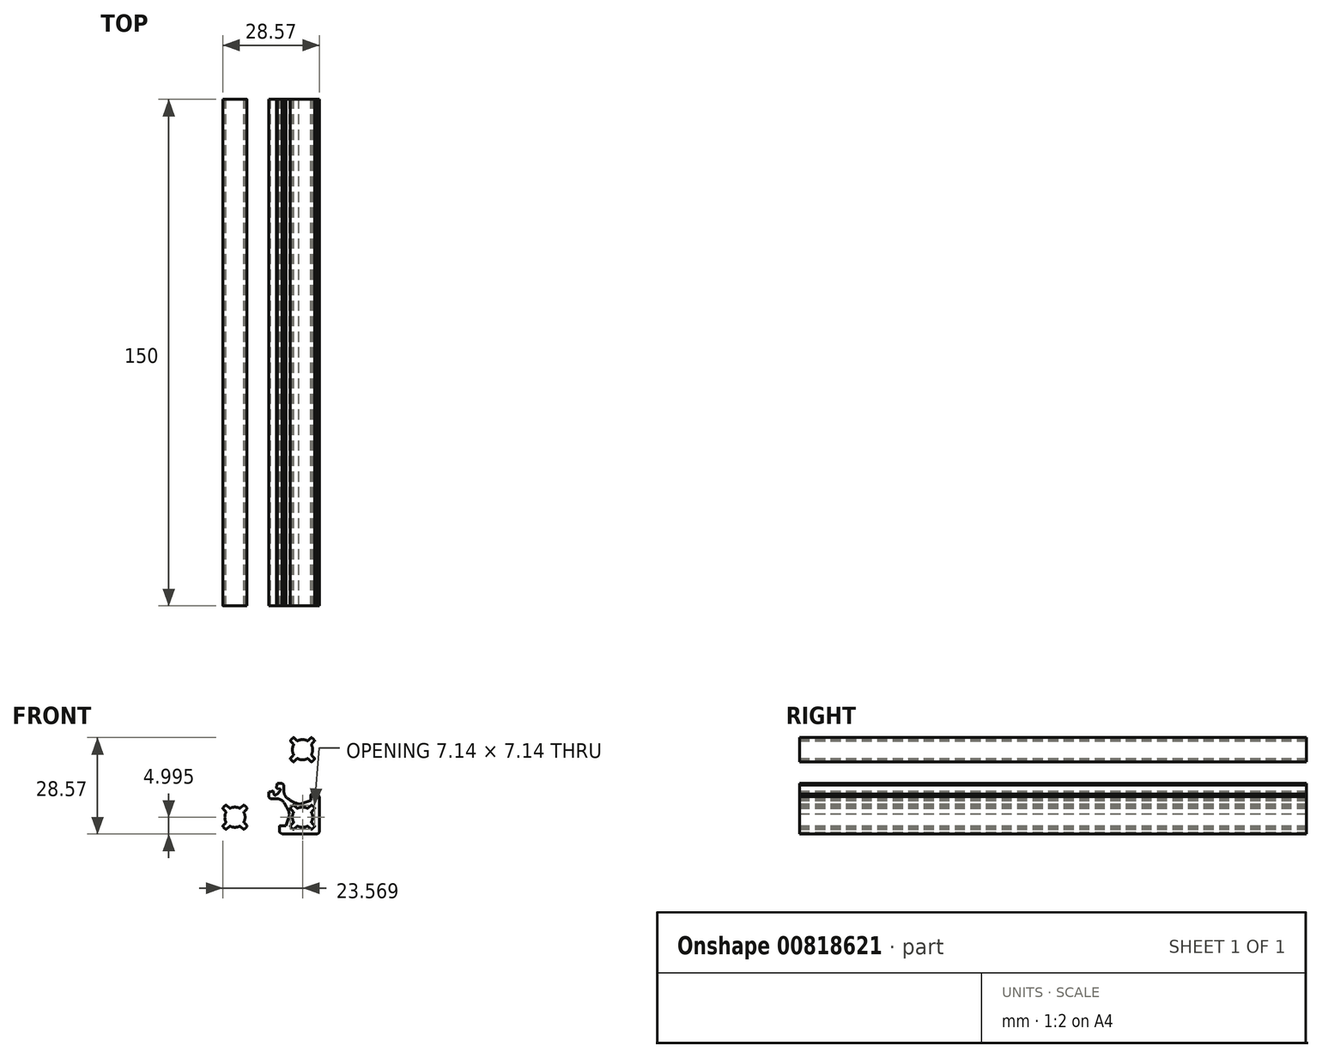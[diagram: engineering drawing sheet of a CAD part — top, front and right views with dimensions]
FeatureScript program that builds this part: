
annotation { "Feature Type Name" : "Feature", "Feature Type Description" : "" }
export const myFeature = defineFeature(function(context is Context, id is Id, definition is map)
    precondition{}
    {
        {
            var Q0;
            Q0=qCreatedBy(makeId("Front.planeOp"),FACE);
            var sketch = newSketch(context, id + "F0", { "sketchPlane" : qUnion([Q0])});
            skLineSegment(sketch, "E0", {"start": v(-2.82, -20.25) * mm, "end": v(-2.82, -15.85) * mm});
            skLineSegment(sketch, "E1", {"start": v(-5.02, -18.05) * mm, "end": v(-0.62, -18.05) * mm});
            skArc(sketch, "E2", {"start": v(-5.5, -19.39) * mm, "mid": v(-5.48, -19.57) * mm, "end": v(-5.56, -19.74) * mm});
            skLineSegment(sketch, "E3", {"start": v(-5.56, -19.74) * mm, "end": v(-6.3, -20.48) * mm});
            skArc(sketch, "E4", {"start": v(-6.3, -20.48) * mm, "mid": v(-6.4, -20.67) * mm, "end": v(-6.32, -20.88) * mm});
            skArc(sketch, "E5", {"start": v(-6.32, -20.88) * mm, "mid": v(-6, -21.24) * mm, "end": v(-5.64, -21.56) * mm});
            skArc(sketch, "E6", {"start": v(-5.64, -21.56) * mm, "mid": v(-5.44, -21.62) * mm, "end": v(-5.24, -21.54) * mm});
            skLineSegment(sketch, "E7", {"start": v(-5.24, -21.54) * mm, "end": v(-4.5, -20.8) * mm});
            skArc(sketch, "E8", {"start": v(-4.5, -20.8) * mm, "mid": v(-4.34, -20.71) * mm, "end": v(-4.16, -20.74) * mm});
            skArc(sketch, "E9", {"start": v(-4.16, -20.74) * mm, "mid": v(-2.82, -21.05) * mm, "end": v(-1.48, -20.74) * mm});
            skArc(sketch, "E10", {"start": v(-1.48, -20.74) * mm, "mid": v(-1.3, -20.71) * mm, "end": v(-1.14, -20.8) * mm});
            skLineSegment(sketch, "E11", {"start": v(-1.14, -20.8) * mm, "end": v(-0.4, -21.54) * mm});
            skArc(sketch, "E12", {"start": v(-0.4, -21.54) * mm, "mid": v(-0.2, -21.62) * mm, "end": v(0, -21.56) * mm});
            skArc(sketch, "E13", {"start": v(0, -21.56) * mm, "mid": v(0.36, -21.24) * mm, "end": v(0.68, -20.88) * mm});
            skArc(sketch, "E14", {"start": v(0.68, -20.88) * mm, "mid": v(0.75, -20.67) * mm, "end": v(0.66, -20.48) * mm});
            skLineSegment(sketch, "E15", {"start": v(0.66, -20.48) * mm, "end": v(-0.08, -19.74) * mm});
            skArc(sketch, "E16", {"start": v(-0.08, -19.74) * mm, "mid": v(-0.16, -19.57) * mm, "end": v(-0.13, -19.39) * mm});
            skArc(sketch, "E17", {"start": v(-0.13, -19.39) * mm, "mid": v(0.18, -18.05) * mm, "end": v(-0.13, -16.72) * mm});
            skArc(sketch, "E18", {"start": v(-0.13, -16.72) * mm, "mid": v(-0.16, -16.54) * mm, "end": v(-0.08, -16.37) * mm});
            skLineSegment(sketch, "E19", {"start": v(-0.08, -16.37) * mm, "end": v(0.66, -15.63) * mm});
            skArc(sketch, "E20", {"start": v(0.66, -15.63) * mm, "mid": v(0.75, -15.44) * mm, "end": v(0.68, -15.23) * mm});
            skArc(sketch, "E21", {"start": v(0.68, -15.23) * mm, "mid": v(0.36, -14.87) * mm, "end": v(0, -14.55) * mm});
            skArc(sketch, "E22", {"start": v(0, -14.55) * mm, "mid": v(-0.2, -14.48) * mm, "end": v(-0.4, -14.57) * mm});
            skLineSegment(sketch, "E23", {"start": v(-0.4, -14.57) * mm, "end": v(-1.14, -15.31) * mm});
            skArc(sketch, "E24", {"start": v(-1.14, -15.31) * mm, "mid": v(-1.3, -15.4) * mm, "end": v(-1.48, -15.37) * mm});
            skArc(sketch, "E25", {"start": v(-1.48, -15.37) * mm, "mid": v(-2.82, -15.05) * mm, "end": v(-4.16, -15.37) * mm});
            skArc(sketch, "E26", {"start": v(-4.16, -15.37) * mm, "mid": v(-4.34, -15.4) * mm, "end": v(-4.5, -15.31) * mm});
            skLineSegment(sketch, "E27", {"start": v(-4.5, -15.31) * mm, "end": v(-5.24, -14.57) * mm});
            skArc(sketch, "E28", {"start": v(-5.24, -14.57) * mm, "mid": v(-5.44, -14.48) * mm, "end": v(-5.64, -14.55) * mm});
            skArc(sketch, "E29", {"start": v(-5.64, -14.55) * mm, "mid": v(-6, -14.87) * mm, "end": v(-6.32, -15.23) * mm});
            skArc(sketch, "E30", {"start": v(-6.32, -15.23) * mm, "mid": v(-6.4, -15.44) * mm, "end": v(-6.3, -15.63) * mm});
            skLineSegment(sketch, "E31", {"start": v(-6.3, -15.63) * mm, "end": v(-5.56, -16.37) * mm});
            skArc(sketch, "E32", {"start": v(-5.56, -16.37) * mm, "mid": v(-5.48, -16.54) * mm, "end": v(-5.5, -16.72) * mm});
            skArc(sketch, "E33", {"start": v(-5.5, -16.72) * mm, "mid": v(-5.82, -18.05) * mm, "end": v(-5.5, -19.39) * mm});
            skLineSegment(sketch, "E34", {"start": v(-5.02, -38.05) * mm, "end": v(-0.62, -38.05) * mm});
            skLineSegment(sketch, "E35", {"start": v(-2.82, -35.85) * mm, "end": v(-2.82, -40.25) * mm});
            skArc(sketch, "E36", {"start": v(-5.5, -36.72) * mm, "mid": v(-5.48, -36.54) * mm, "end": v(-5.56, -36.37) * mm});
            skLineSegment(sketch, "E37", {"start": v(-5.56, -36.37) * mm, "end": v(-6.3, -35.63) * mm});
            skArc(sketch, "E38", {"start": v(-6.3, -35.63) * mm, "mid": v(-6.4, -35.44) * mm, "end": v(-6.33, -35.23) * mm});
            skArc(sketch, "E39", {"start": v(-6.33, -35.23) * mm, "mid": v(-6, -34.87) * mm, "end": v(-5.64, -34.55) * mm});
            skArc(sketch, "E40", {"start": v(-5.64, -34.55) * mm, "mid": v(-5.44, -34.48) * mm, "end": v(-5.24, -34.57) * mm});
            skLineSegment(sketch, "E41", {"start": v(-5.24, -34.57) * mm, "end": v(-4.5, -35.31) * mm});
            skArc(sketch, "E42", {"start": v(-4.5, -35.31) * mm, "mid": v(-4.34, -35.4) * mm, "end": v(-4.16, -35.37) * mm});
            skArc(sketch, "E43", {"start": v(-4.16, -35.37) * mm, "mid": v(-2.82, -35.05) * mm, "end": v(-1.48, -35.37) * mm});
            skArc(sketch, "E44", {"start": v(-1.48, -35.37) * mm, "mid": v(-1.3, -35.4) * mm, "end": v(-1.14, -35.31) * mm});
            skLineSegment(sketch, "E45", {"start": v(-1.14, -35.31) * mm, "end": v(-0.4, -34.57) * mm});
            skArc(sketch, "E46", {"start": v(-0.4, -34.57) * mm, "mid": v(-0.2, -34.48) * mm, "end": v(0, -34.55) * mm});
            skArc(sketch, "E47", {"start": v(0, -34.55) * mm, "mid": v(0.36, -34.87) * mm, "end": v(0.68, -35.23) * mm});
            skArc(sketch, "E48", {"start": v(0.68, -35.23) * mm, "mid": v(0.75, -35.44) * mm, "end": v(0.66, -35.63) * mm});
            skLineSegment(sketch, "E49", {"start": v(0.66, -35.63) * mm, "end": v(-0.08, -36.37) * mm});
            skArc(sketch, "E50", {"start": v(-0.08, -36.37) * mm, "mid": v(-0.16, -36.54) * mm, "end": v(-0.13, -36.72) * mm});
            skArc(sketch, "E51", {"start": v(-0.13, -36.72) * mm, "mid": v(0.18, -38.05) * mm, "end": v(-0.14, -39.4) * mm});
            skArc(sketch, "E52", {"start": v(-0.14, -39.4) * mm, "mid": v(-0.16, -39.57) * mm, "end": v(-0.08, -39.74) * mm});
            skLineSegment(sketch, "E53", {"start": v(-0.08, -39.74) * mm, "end": v(0.66, -40.48) * mm});
            skArc(sketch, "E54", {"start": v(0.66, -40.48) * mm, "mid": v(0.75, -40.67) * mm, "end": v(0.68, -40.88) * mm});
            skArc(sketch, "E55", {"start": v(0.68, -40.88) * mm, "mid": v(0.36, -41.24) * mm, "end": v(0, -41.56) * mm});
            skArc(sketch, "E56", {"start": v(0, -41.56) * mm, "mid": v(-0.2, -41.63) * mm, "end": v(-0.4, -41.54) * mm});
            skLineSegment(sketch, "E57", {"start": v(-0.4, -41.54) * mm, "end": v(-1.14, -40.8) * mm});
            skArc(sketch, "E58", {"start": v(-1.14, -40.8) * mm, "mid": v(-1.3, -40.71) * mm, "end": v(-1.49, -40.74) * mm});
            skArc(sketch, "E59", {"start": v(-1.49, -40.74) * mm, "mid": v(-2.82, -41.05) * mm, "end": v(-4.16, -40.74) * mm});
            skArc(sketch, "E60", {"start": v(-4.16, -40.74) * mm, "mid": v(-4.34, -40.71) * mm, "end": v(-4.5, -40.8) * mm});
            skLineSegment(sketch, "E61", {"start": v(-4.5, -40.8) * mm, "end": v(-5.24, -41.54) * mm});
            skArc(sketch, "E62", {"start": v(-5.24, -41.54) * mm, "mid": v(-5.44, -41.62) * mm, "end": v(-5.64, -41.56) * mm});
            skArc(sketch, "E63", {"start": v(-5.64, -41.56) * mm, "mid": v(-6, -41.24) * mm, "end": v(-6.33, -40.88) * mm});
            skArc(sketch, "E64", {"start": v(-6.33, -40.88) * mm, "mid": v(-6.4, -40.67) * mm, "end": v(-6.3, -40.48) * mm});
            skLineSegment(sketch, "E65", {"start": v(-6.3, -40.48) * mm, "end": v(-5.56, -39.74) * mm});
            skArc(sketch, "E66", {"start": v(-5.56, -39.74) * mm, "mid": v(-5.48, -39.57) * mm, "end": v(-5.5, -39.4) * mm});
            skArc(sketch, "E67", {"start": v(-5.5, -39.4) * mm, "mid": v(-5.82, -38.05) * mm, "end": v(-5.5, -36.72) * mm});
            skArc(sketch, "E68", {"start": v(-20.13, -36.72) * mm, "mid": v(-20.16, -36.54) * mm, "end": v(-20.07, -36.37) * mm});
            skLineSegment(sketch, "E69", {"start": v(-20.07, -36.37) * mm, "end": v(-19.33, -35.63) * mm});
            skArc(sketch, "E70", {"start": v(-19.33, -35.63) * mm, "mid": v(-19.25, -35.44) * mm, "end": v(-19.31, -35.23) * mm});
            skArc(sketch, "E71", {"start": v(-19.31, -35.23) * mm, "mid": v(-19.64, -34.87) * mm, "end": v(-20, -34.55) * mm});
            skArc(sketch, "E72", {"start": v(-20, -34.55) * mm, "mid": v(-20.2, -34.48) * mm, "end": v(-20.4, -34.57) * mm});
            skLineSegment(sketch, "E73", {"start": v(-20.4, -34.57) * mm, "end": v(-21.14, -35.31) * mm});
            skArc(sketch, "E74", {"start": v(-21.14, -35.31) * mm, "mid": v(-21.3, -35.4) * mm, "end": v(-21.48, -35.37) * mm});
            skArc(sketch, "E75", {"start": v(-21.48, -35.37) * mm, "mid": v(-22.82, -35.05) * mm, "end": v(-24.15, -35.37) * mm});
            skArc(sketch, "E76", {"start": v(-24.15, -35.37) * mm, "mid": v(-24.34, -35.4) * mm, "end": v(-24.5, -35.31) * mm});
            skLineSegment(sketch, "E77", {"start": v(-24.5, -35.31) * mm, "end": v(-25.24, -34.57) * mm});
            skArc(sketch, "E78", {"start": v(-25.24, -34.57) * mm, "mid": v(-25.44, -34.48) * mm, "end": v(-25.64, -34.55) * mm});
            skArc(sketch, "E79", {"start": v(-25.64, -34.55) * mm, "mid": v(-26, -34.87) * mm, "end": v(-26.32, -35.23) * mm});
            skArc(sketch, "E80", {"start": v(-26.32, -35.23) * mm, "mid": v(-26.39, -35.44) * mm, "end": v(-26.3, -35.63) * mm});
            skLineSegment(sketch, "E81", {"start": v(-26.3, -35.63) * mm, "end": v(-25.56, -36.37) * mm});
            skArc(sketch, "E82", {"start": v(-25.56, -36.37) * mm, "mid": v(-25.48, -36.54) * mm, "end": v(-25.5, -36.72) * mm});
            skArc(sketch, "E83", {"start": v(-25.5, -36.72) * mm, "mid": v(-25.82, -38.05) * mm, "end": v(-25.5, -39.4) * mm});
            skArc(sketch, "E84", {"start": v(-25.5, -39.4) * mm, "mid": v(-25.48, -39.57) * mm, "end": v(-25.56, -39.74) * mm});
            skLineSegment(sketch, "E85", {"start": v(-25.56, -39.74) * mm, "end": v(-26.3, -40.48) * mm});
            skArc(sketch, "E86", {"start": v(-26.3, -40.48) * mm, "mid": v(-26.39, -40.67) * mm, "end": v(-26.32, -40.88) * mm});
            skArc(sketch, "E87", {"start": v(-26.32, -40.88) * mm, "mid": v(-26, -41.24) * mm, "end": v(-25.64, -41.56) * mm});
            skArc(sketch, "E88", {"start": v(-25.64, -41.56) * mm, "mid": v(-25.44, -41.63) * mm, "end": v(-25.24, -41.54) * mm});
            skLineSegment(sketch, "E89", {"start": v(-25.24, -41.54) * mm, "end": v(-24.5, -40.8) * mm});
            skArc(sketch, "E90", {"start": v(-24.5, -40.8) * mm, "mid": v(-24.33, -40.71) * mm, "end": v(-24.15, -40.74) * mm});
            skArc(sketch, "E91", {"start": v(-24.15, -40.74) * mm, "mid": v(-22.82, -41.05) * mm, "end": v(-21.48, -40.74) * mm});
            skArc(sketch, "E92", {"start": v(-21.48, -40.74) * mm, "mid": v(-21.3, -40.71) * mm, "end": v(-21.14, -40.8) * mm});
            skLineSegment(sketch, "E93", {"start": v(-21.14, -40.8) * mm, "end": v(-20.4, -41.54) * mm});
            skArc(sketch, "E94", {"start": v(-20.4, -41.54) * mm, "mid": v(-20.2, -41.62) * mm, "end": v(-20, -41.56) * mm});
            skArc(sketch, "E95", {"start": v(-20, -41.56) * mm, "mid": v(-19.63, -41.24) * mm, "end": v(-19.31, -40.88) * mm});
            skArc(sketch, "E96", {"start": v(-19.31, -40.88) * mm, "mid": v(-19.25, -40.67) * mm, "end": v(-19.33, -40.48) * mm});
            skLineSegment(sketch, "E97", {"start": v(-19.33, -40.48) * mm, "end": v(-20.07, -39.74) * mm});
            skArc(sketch, "E98", {"start": v(-20.07, -39.74) * mm, "mid": v(-20.16, -39.57) * mm, "end": v(-20.13, -39.4) * mm});
            skArc(sketch, "E99", {"start": v(-20.13, -39.4) * mm, "mid": v(-19.82, -38.05) * mm, "end": v(-20.13, -36.72) * mm});
            skLineSegment(sketch, "E100", {"start": v(-22.82, -35.85) * mm, "end": v(-22.82, -40.25) * mm});
            skLineSegment(sketch, "E101", {"start": v(-20.62, -38.05) * mm, "end": v(-25.02, -38.05) * mm});
            skLineSegment(sketch, "E102", {"start": v(-20.62, -18.05) * mm, "end": v(-25.02, -18.05) * mm});
            skLineSegment(sketch, "E103", {"start": v(-22.82, -20.25) * mm, "end": v(-22.82, -15.85) * mm});
            skLineSegment(sketch, "E104", {"start": v(2.64, -28.05) * mm, "end": v(-29.04, -28.05) * mm});
            skLineSegment(sketch, "E105", {"start": v(-12.82, -44) * mm, "end": v(-12.82, -12.06) * mm});
            skArc(sketch, "E106", {"start": v(-9.58, -26.47) * mm, "mid": v(-9.36, -26.3) * mm, "end": v(-9.38, -26.02) * mm});
            skArc(sketch, "E107", {"start": v(-9.38, -26.02) * mm, "mid": v(-10, -25.23) * mm, "end": v(-10.78, -24.61) * mm});
            skArc(sketch, "E108", {"start": v(-10.78, -24.61) * mm, "mid": v(-11.06, -24.6) * mm, "end": v(-11.23, -24.82) * mm});
            skLineSegment(sketch, "E109", {"start": v(-11.23, -24.82) * mm, "end": v(-11.37, -25.56) * mm});
            skArc(sketch, "E110", {"start": v(-11.37, -25.56) * mm, "mid": v(-11.52, -25.77) * mm, "end": v(-11.78, -25.78) * mm});
            skArc(sketch, "E111", {"start": v(-11.78, -25.78) * mm, "mid": v(-12.82, -25.55) * mm, "end": v(-13.85, -25.78) * mm});
            skArc(sketch, "E112", {"start": v(-13.85, -25.78) * mm, "mid": v(-14.11, -25.77) * mm, "end": v(-14.27, -25.56) * mm});
            skLineSegment(sketch, "E113", {"start": v(-14.27, -25.56) * mm, "end": v(-14.4, -24.82) * mm});
            skArc(sketch, "E114", {"start": v(-14.4, -24.82) * mm, "mid": v(-14.57, -24.6) * mm, "end": v(-14.85, -24.61) * mm});
            skArc(sketch, "E115", {"start": v(-14.85, -24.61) * mm, "mid": v(-15.65, -25.23) * mm, "end": v(-16.26, -26.02) * mm});
            skArc(sketch, "E116", {"start": v(-16.26, -26.02) * mm, "mid": v(-16.27, -26.3) * mm, "end": v(-16.06, -26.47) * mm});
            skLineSegment(sketch, "E117", {"start": v(-16.06, -26.47) * mm, "end": v(-15.31, -26.6) * mm});
            skArc(sketch, "E118", {"start": v(-15.31, -26.6) * mm, "mid": v(-15.1, -26.76) * mm, "end": v(-15.1, -27.02) * mm});
            skArc(sketch, "E119", {"start": v(-15.1, -27.02) * mm, "mid": v(-15.32, -28.05) * mm, "end": v(-15.1, -29.09) * mm});
            skArc(sketch, "E120", {"start": v(-15.1, -29.09) * mm, "mid": v(-15.1, -29.35) * mm, "end": v(-15.31, -29.5) * mm});
            skLineSegment(sketch, "E121", {"start": v(-15.31, -29.5) * mm, "end": v(-16.06, -29.64) * mm});
            skArc(sketch, "E122", {"start": v(-16.06, -29.64) * mm, "mid": v(-16.27, -29.81) * mm, "end": v(-16.26, -30.09) * mm});
            skArc(sketch, "E123", {"start": v(-16.26, -30.09) * mm, "mid": v(-15.65, -30.88) * mm, "end": v(-14.85, -31.5) * mm});
            skArc(sketch, "E124", {"start": v(-14.85, -31.5) * mm, "mid": v(-14.57, -31.51) * mm, "end": v(-14.4, -31.3) * mm});
            skLineSegment(sketch, "E125", {"start": v(-14.4, -31.3) * mm, "end": v(-14.27, -30.55) * mm});
            skArc(sketch, "E126", {"start": v(-14.27, -30.55) * mm, "mid": v(-14.11, -30.34) * mm, "end": v(-13.85, -30.33) * mm});
            skArc(sketch, "E127", {"start": v(-13.85, -30.33) * mm, "mid": v(-12.82, -30.55) * mm, "end": v(-11.78, -30.33) * mm});
            skArc(sketch, "E128", {"start": v(-11.78, -30.33) * mm, "mid": v(-11.52, -30.34) * mm, "end": v(-11.37, -30.55) * mm});
            skLineSegment(sketch, "E129", {"start": v(-11.37, -30.55) * mm, "end": v(-11.23, -31.3) * mm});
            skArc(sketch, "E130", {"start": v(-11.23, -31.3) * mm, "mid": v(-11.06, -31.51) * mm, "end": v(-10.78, -31.5) * mm});
            skArc(sketch, "E131", {"start": v(-10.78, -31.5) * mm, "mid": v(-10, -30.88) * mm, "end": v(-9.38, -30.09) * mm});
            skArc(sketch, "E132", {"start": v(-9.38, -30.09) * mm, "mid": v(-9.36, -29.81) * mm, "end": v(-9.58, -29.64) * mm});
            skLineSegment(sketch, "E133", {"start": v(-9.58, -29.64) * mm, "end": v(-10.32, -29.5) * mm});
            skArc(sketch, "E134", {"start": v(-10.32, -29.5) * mm, "mid": v(-10.53, -29.35) * mm, "end": v(-10.54, -29.09) * mm});
            skArc(sketch, "E135", {"start": v(-10.54, -29.09) * mm, "mid": v(-10.32, -28.05) * mm, "end": v(-10.54, -27.02) * mm});
            skArc(sketch, "E136", {"start": v(-10.54, -27.02) * mm, "mid": v(-10.53, -26.76) * mm, "end": v(-10.32, -26.6) * mm});
            skLineSegment(sketch, "E137", {"start": v(-10.32, -26.6) * mm, "end": v(-9.58, -26.47) * mm});
            skArc(sketch, "E138", {"start": v(-20.13, -19.39) * mm, "mid": v(-20.16, -19.57) * mm, "end": v(-20.08, -19.74) * mm});
            skLineSegment(sketch, "E139", {"start": v(-20.08, -19.74) * mm, "end": v(-19.33, -20.48) * mm});
            skArc(sketch, "E140", {"start": v(-19.33, -20.48) * mm, "mid": v(-19.25, -20.67) * mm, "end": v(-19.31, -20.88) * mm});
            skArc(sketch, "E141", {"start": v(-19.31, -20.88) * mm, "mid": v(-19.64, -21.24) * mm, "end": v(-20, -21.56) * mm});
            skArc(sketch, "E142", {"start": v(-20, -21.56) * mm, "mid": v(-20.2, -21.62) * mm, "end": v(-20.4, -21.54) * mm});
            skLineSegment(sketch, "E143", {"start": v(-20.4, -21.54) * mm, "end": v(-21.14, -20.8) * mm});
            skArc(sketch, "E144", {"start": v(-21.14, -20.8) * mm, "mid": v(-21.3, -20.71) * mm, "end": v(-21.48, -20.74) * mm});
            skArc(sketch, "E145", {"start": v(-21.48, -20.74) * mm, "mid": v(-22.82, -21.05) * mm, "end": v(-24.15, -20.74) * mm});
            skArc(sketch, "E146", {"start": v(-24.15, -20.74) * mm, "mid": v(-24.34, -20.71) * mm, "end": v(-24.5, -20.8) * mm});
            skLineSegment(sketch, "E147", {"start": v(-24.5, -20.8) * mm, "end": v(-25.24, -21.54) * mm});
            skArc(sketch, "E148", {"start": v(-25.24, -21.54) * mm, "mid": v(-25.44, -21.62) * mm, "end": v(-25.64, -21.56) * mm});
            skArc(sketch, "E149", {"start": v(-25.64, -21.56) * mm, "mid": v(-26, -21.24) * mm, "end": v(-26.32, -20.88) * mm});
            skArc(sketch, "E150", {"start": v(-26.32, -20.88) * mm, "mid": v(-26.39, -20.67) * mm, "end": v(-26.3, -20.48) * mm});
            skLineSegment(sketch, "E151", {"start": v(-26.3, -20.48) * mm, "end": v(-25.56, -19.74) * mm});
            skArc(sketch, "E152", {"start": v(-25.56, -19.74) * mm, "mid": v(-25.48, -19.57) * mm, "end": v(-25.5, -19.39) * mm});
            skArc(sketch, "E153", {"start": v(-25.5, -19.39) * mm, "mid": v(-25.82, -18.05) * mm, "end": v(-25.5, -16.72) * mm});
            skArc(sketch, "E154", {"start": v(-25.5, -16.72) * mm, "mid": v(-25.48, -16.54) * mm, "end": v(-25.56, -16.37) * mm});
            skLineSegment(sketch, "E155", {"start": v(-25.56, -16.37) * mm, "end": v(-26.3, -15.63) * mm});
            skArc(sketch, "E156", {"start": v(-26.3, -15.63) * mm, "mid": v(-26.39, -15.44) * mm, "end": v(-26.32, -15.23) * mm});
            skArc(sketch, "E157", {"start": v(-26.32, -15.23) * mm, "mid": v(-26, -14.87) * mm, "end": v(-25.64, -14.55) * mm});
            skArc(sketch, "E158", {"start": v(-25.64, -14.55) * mm, "mid": v(-25.44, -14.48) * mm, "end": v(-25.24, -14.57) * mm});
            skLineSegment(sketch, "E159", {"start": v(-25.24, -14.57) * mm, "end": v(-24.5, -15.31) * mm});
            skArc(sketch, "E160", {"start": v(-24.5, -15.31) * mm, "mid": v(-24.34, -15.4) * mm, "end": v(-24.15, -15.37) * mm});
            skArc(sketch, "E161", {"start": v(-24.15, -15.37) * mm, "mid": v(-22.82, -15.05) * mm, "end": v(-21.48, -15.37) * mm});
            skArc(sketch, "E162", {"start": v(-21.48, -15.37) * mm, "mid": v(-21.3, -15.4) * mm, "end": v(-21.14, -15.31) * mm});
            skLineSegment(sketch, "E163", {"start": v(-21.14, -15.31) * mm, "end": v(-20.4, -14.57) * mm});
            skArc(sketch, "E164", {"start": v(-20.4, -14.57) * mm, "mid": v(-20.2, -14.48) * mm, "end": v(-20, -14.55) * mm});
            skArc(sketch, "E165", {"start": v(-20, -14.55) * mm, "mid": v(-19.64, -14.87) * mm, "end": v(-19.31, -15.23) * mm});
            skArc(sketch, "E166", {"start": v(-19.31, -15.23) * mm, "mid": v(-19.25, -15.44) * mm, "end": v(-19.33, -15.63) * mm});
            skLineSegment(sketch, "E167", {"start": v(-19.33, -15.63) * mm, "end": v(-20.08, -16.37) * mm});
            skArc(sketch, "E168", {"start": v(-20.08, -16.37) * mm, "mid": v(-20.16, -16.54) * mm, "end": v(-20.13, -16.72) * mm});
            skArc(sketch, "E169", {"start": v(-20.13, -16.72) * mm, "mid": v(-19.82, -18.05) * mm, "end": v(-20.13, -19.39) * mm});
            skLineSegment(sketch, "E170", {"start": v(-8.87, -43.05) * mm, "end": v(-9.67, -42.55) * mm});
            skLineSegment(sketch, "E171", {"start": v(-9.67, -42.55) * mm, "end": v(-9.67, -40.85) * mm});
            skArc(sketch, "E172", {"start": v(-9.67, -40.85) * mm, "mid": v(-9.58, -40.64) * mm, "end": v(-9.37, -40.55) * mm});
            skLineSegment(sketch, "E173", {"start": v(-9.37, -40.55) * mm, "end": v(-7.72, -40.55) * mm});
            skLineSegment(sketch, "E174", {"start": v(-7.72, -40.55) * mm, "end": v(-6.73, -37.5) * mm});
            skArc(sketch, "E175", {"start": v(-6.73, -37.5) * mm, "mid": v(-6.68, -37.24) * mm, "end": v(-6.7, -36.98) * mm});
            skArc(sketch, "E176", {"start": v(-6.7, -36.98) * mm, "mid": v(-7.54, -34.94) * mm, "end": v(-8.81, -33.14) * mm});
            skArc(sketch, "E177", {"start": v(-8.81, -33.14) * mm, "mid": v(-9.66, -32.7) * mm, "end": v(-10.6, -32.55) * mm});
            skLineSegment(sketch, "E178", {"start": v(-10.6, -32.55) * mm, "end": v(-12.32, -32.55) * mm});
            skLineSegment(sketch, "E179", {"start": v(-12.32, -32.55) * mm, "end": v(-12.82, -32.05) * mm});
            skLineSegment(sketch, "E180", {"start": v(-12.82, -32.05) * mm, "end": v(-13.32, -32.55) * mm});
            skLineSegment(sketch, "E181", {"start": v(-13.32, -32.55) * mm, "end": v(-15.04, -32.55) * mm});
            skArc(sketch, "E182", {"start": v(-15.04, -32.55) * mm, "mid": v(-15.98, -32.7) * mm, "end": v(-16.82, -33.14) * mm});
            skArc(sketch, "E183", {"start": v(-16.82, -33.14) * mm, "mid": v(-18.1, -34.94) * mm, "end": v(-18.93, -36.98) * mm});
            skArc(sketch, "E184", {"start": v(-18.93, -36.98) * mm, "mid": v(-18.95, -37.24) * mm, "end": v(-18.9, -37.5) * mm});
            skLineSegment(sketch, "E185", {"start": v(-18.9, -37.5) * mm, "end": v(-17.92, -40.55) * mm});
            skLineSegment(sketch, "E186", {"start": v(-17.92, -40.55) * mm, "end": v(-16.27, -40.55) * mm});
            skArc(sketch, "E187", {"start": v(-16.27, -40.55) * mm, "mid": v(-16.06, -40.64) * mm, "end": v(-15.97, -40.85) * mm});
            skLineSegment(sketch, "E188", {"start": v(-15.97, -40.85) * mm, "end": v(-15.97, -42.55) * mm});
            skLineSegment(sketch, "E189", {"start": v(-15.97, -42.55) * mm, "end": v(-16.77, -43.05) * mm});
            skLineSegment(sketch, "E190", {"start": v(-16.77, -43.05) * mm, "end": v(-26.82, -43.05) * mm});
            skArc(sketch, "E191", {"start": v(-26.82, -43.05) * mm, "mid": v(-27.52, -42.76) * mm, "end": v(-27.82, -42.05) * mm});
            skLineSegment(sketch, "E192", {"start": v(-27.82, -42.05) * mm, "end": v(-27.82, -32) * mm});
            skLineSegment(sketch, "E193", {"start": v(-27.82, -32) * mm, "end": v(-27.32, -31.2) * mm});
            skLineSegment(sketch, "E194", {"start": v(-27.32, -31.2) * mm, "end": v(-25.62, -31.2) * mm});
            skArc(sketch, "E195", {"start": v(-25.62, -31.2) * mm, "mid": v(-25.4, -31.3) * mm, "end": v(-25.32, -31.5) * mm});
            skLineSegment(sketch, "E196", {"start": v(-25.32, -31.5) * mm, "end": v(-25.32, -33.15) * mm});
            skLineSegment(sketch, "E197", {"start": v(-25.32, -33.15) * mm, "end": v(-22.27, -34.14) * mm});
            skArc(sketch, "E198", {"start": v(-22.27, -34.14) * mm, "mid": v(-22, -34.19) * mm, "end": v(-21.75, -34.17) * mm});
            skArc(sketch, "E199", {"start": v(-21.75, -34.17) * mm, "mid": v(-19.7, -33.33) * mm, "end": v(-17.9, -32.06) * mm});
            skArc(sketch, "E200", {"start": v(-17.9, -32.06) * mm, "mid": v(-17.47, -31.21) * mm, "end": v(-17.32, -30.27) * mm});
            skLineSegment(sketch, "E201", {"start": v(-17.32, -30.27) * mm, "end": v(-17.32, -28.55) * mm});
            skLineSegment(sketch, "E202", {"start": v(-17.32, -28.55) * mm, "end": v(-16.82, -28.05) * mm});
            skLineSegment(sketch, "E203", {"start": v(-16.82, -28.05) * mm, "end": v(-17.32, -27.55) * mm});
            skLineSegment(sketch, "E204", {"start": v(-17.32, -27.55) * mm, "end": v(-17.32, -25.84) * mm});
            skArc(sketch, "E205", {"start": v(-17.32, -25.84) * mm, "mid": v(-17.47, -24.9) * mm, "end": v(-17.9, -24.05) * mm});
            skArc(sketch, "E206", {"start": v(-17.9, -24.05) * mm, "mid": v(-19.7, -22.78) * mm, "end": v(-21.75, -21.94) * mm});
            skArc(sketch, "E207", {"start": v(-21.75, -21.94) * mm, "mid": v(-22, -21.92) * mm, "end": v(-22.27, -21.97) * mm});
            skLineSegment(sketch, "E208", {"start": v(-22.27, -21.97) * mm, "end": v(-25.32, -22.95) * mm});
            skLineSegment(sketch, "E209", {"start": v(-25.32, -22.95) * mm, "end": v(-25.32, -24.6) * mm});
            skArc(sketch, "E210", {"start": v(-25.32, -24.6) * mm, "mid": v(-25.4, -24.82) * mm, "end": v(-25.62, -24.9) * mm});
            skLineSegment(sketch, "E211", {"start": v(-25.62, -24.9) * mm, "end": v(-27.32, -24.9) * mm});
            skLineSegment(sketch, "E212", {"start": v(-27.32, -24.9) * mm, "end": v(-27.82, -24.1) * mm});
            skLineSegment(sketch, "E213", {"start": v(-27.82, -24.1) * mm, "end": v(-27.82, -14.05) * mm});
            skArc(sketch, "E214", {"start": v(-27.82, -14.05) * mm, "mid": v(-27.52, -13.35) * mm, "end": v(-26.82, -13.05) * mm});
            skLineSegment(sketch, "E215", {"start": v(-26.82, -13.05) * mm, "end": v(-16.77, -13.05) * mm});
            skLineSegment(sketch, "E216", {"start": v(-16.77, -13.05) * mm, "end": v(-15.97, -13.55) * mm});
            skLineSegment(sketch, "E217", {"start": v(-15.97, -13.55) * mm, "end": v(-15.97, -15.25) * mm});
            skArc(sketch, "E218", {"start": v(-15.97, -15.25) * mm, "mid": v(-16.06, -15.47) * mm, "end": v(-16.27, -15.55) * mm});
            skLineSegment(sketch, "E219", {"start": v(-16.27, -15.55) * mm, "end": v(-17.92, -15.55) * mm});
            skLineSegment(sketch, "E220", {"start": v(-17.92, -15.55) * mm, "end": v(-18.9, -18.6) * mm});
            skArc(sketch, "E221", {"start": v(-18.9, -18.6) * mm, "mid": v(-18.95, -18.86) * mm, "end": v(-18.93, -19.13) * mm});
            skArc(sketch, "E222", {"start": v(-18.93, -19.13) * mm, "mid": v(-18.1, -21.16) * mm, "end": v(-16.82, -22.96) * mm});
            skArc(sketch, "E223", {"start": v(-16.82, -22.96) * mm, "mid": v(-15.98, -23.4) * mm, "end": v(-15.04, -23.55) * mm});
            skLineSegment(sketch, "E224", {"start": v(-15.04, -23.55) * mm, "end": v(-13.32, -23.55) * mm});
            skLineSegment(sketch, "E225", {"start": v(-13.32, -23.55) * mm, "end": v(-12.82, -24.05) * mm});
            skLineSegment(sketch, "E226", {"start": v(-12.82, -24.05) * mm, "end": v(-12.32, -23.55) * mm});
            skLineSegment(sketch, "E227", {"start": v(-12.32, -23.55) * mm, "end": v(-10.6, -23.55) * mm});
            skArc(sketch, "E228", {"start": v(-10.6, -23.55) * mm, "mid": v(-9.66, -23.4) * mm, "end": v(-8.81, -22.96) * mm});
            skArc(sketch, "E229", {"start": v(-8.81, -22.96) * mm, "mid": v(-7.54, -21.16) * mm, "end": v(-6.7, -19.13) * mm});
            skArc(sketch, "E230", {"start": v(-6.7, -19.13) * mm, "mid": v(-6.68, -18.86) * mm, "end": v(-6.73, -18.6) * mm});
            skLineSegment(sketch, "E231", {"start": v(-6.73, -18.6) * mm, "end": v(-7.72, -15.55) * mm});
            skLineSegment(sketch, "E232", {"start": v(-7.72, -15.55) * mm, "end": v(-9.37, -15.55) * mm});
            skArc(sketch, "E233", {"start": v(-9.37, -15.55) * mm, "mid": v(-9.58, -15.47) * mm, "end": v(-9.67, -15.25) * mm});
            skLineSegment(sketch, "E234", {"start": v(-9.67, -15.25) * mm, "end": v(-9.67, -13.55) * mm});
            skLineSegment(sketch, "E235", {"start": v(-9.67, -13.55) * mm, "end": v(-8.87, -13.05) * mm});
            skLineSegment(sketch, "E236", {"start": v(-8.87, -13.05) * mm, "end": v(1.18, -13.05) * mm});
            skArc(sketch, "E237", {"start": v(1.18, -13.05) * mm, "mid": v(1.89, -13.35) * mm, "end": v(2.18, -14.05) * mm});
            skLineSegment(sketch, "E238", {"start": v(2.18, -14.05) * mm, "end": v(2.18, -24.1) * mm});
            skLineSegment(sketch, "E239", {"start": v(2.18, -24.1) * mm, "end": v(1.68, -24.9) * mm});
            skLineSegment(sketch, "E240", {"start": v(1.68, -24.9) * mm, "end": v(-0.02, -24.9) * mm});
            skArc(sketch, "E241", {"start": v(-0.02, -24.9) * mm, "mid": v(-0.23, -24.82) * mm, "end": v(-0.32, -24.6) * mm});
            skLineSegment(sketch, "E242", {"start": v(-0.32, -24.6) * mm, "end": v(-0.32, -22.95) * mm});
            skLineSegment(sketch, "E243", {"start": v(-0.32, -22.95) * mm, "end": v(-3.37, -21.97) * mm});
            skArc(sketch, "E244", {"start": v(-3.37, -21.97) * mm, "mid": v(-3.63, -21.92) * mm, "end": v(-3.9, -21.94) * mm});
            skArc(sketch, "E245", {"start": v(-3.9, -21.94) * mm, "mid": v(-5.93, -22.78) * mm, "end": v(-7.73, -24.05) * mm});
            skArc(sketch, "E246", {"start": v(-7.73, -24.05) * mm, "mid": v(-8.17, -24.9) * mm, "end": v(-8.32, -25.84) * mm});
            skLineSegment(sketch, "E247", {"start": v(-8.32, -25.84) * mm, "end": v(-8.32, -27.55) * mm});
            skLineSegment(sketch, "E248", {"start": v(-8.32, -27.55) * mm, "end": v(-8.82, -28.05) * mm});
            skLineSegment(sketch, "E249", {"start": v(-8.82, -28.05) * mm, "end": v(-8.32, -28.55) * mm});
            skLineSegment(sketch, "E250", {"start": v(-8.32, -28.55) * mm, "end": v(-8.32, -30.27) * mm});
            skArc(sketch, "E251", {"start": v(-8.32, -30.27) * mm, "mid": v(-8.17, -31.21) * mm, "end": v(-7.73, -32.06) * mm});
            skArc(sketch, "E252", {"start": v(-7.73, -32.06) * mm, "mid": v(-5.93, -33.33) * mm, "end": v(-3.9, -34.17) * mm});
            skArc(sketch, "E253", {"start": v(-3.9, -34.17) * mm, "mid": v(-3.63, -34.19) * mm, "end": v(-3.37, -34.14) * mm});
            skLineSegment(sketch, "E254", {"start": v(-3.37, -34.14) * mm, "end": v(-0.32, -33.15) * mm});
            skLineSegment(sketch, "E255", {"start": v(-0.32, -33.15) * mm, "end": v(-0.32, -31.5) * mm});
            skArc(sketch, "E256", {"start": v(-0.32, -31.5) * mm, "mid": v(-0.23, -31.3) * mm, "end": v(-0.02, -31.2) * mm});
            skLineSegment(sketch, "E257", {"start": v(-0.02, -31.2) * mm, "end": v(1.68, -31.2) * mm});
            skLineSegment(sketch, "E258", {"start": v(1.68, -31.2) * mm, "end": v(2.18, -32) * mm});
            skLineSegment(sketch, "E259", {"start": v(2.18, -32) * mm, "end": v(2.18, -42.05) * mm});
            skArc(sketch, "E260", {"start": v(2.18, -42.05) * mm, "mid": v(1.89, -42.76) * mm, "end": v(1.18, -43.05) * mm});
            skLineSegment(sketch, "E261", {"start": v(1.18, -43.05) * mm, "end": v(-8.87, -43.05) * mm});
            skSolve(sketch);
        }
        {
            var Q0;
            Q0=makeQuery(id+"F0.imprint","IMPRINT",FACE,{"disambiguationData":[TD([[makeQuery(id+"F0.imprint","IMPRINT",EDGE,{"derivedFrom":sQuery(id+"F0.wireOp",EDGE,"E2")}),-1.0]])]});
            var Q1;
            {var subQ1=sQuery(id+"F0.wireOp",EDGE,"E112");Q1=makeQuery(id+"F0.imprint","IMPRINT",FACE,{"disambiguationData":[TD([[makeQuery(id+"F0.imprint","IMPRINT",EDGE,{"derivedFrom":subQ1}),-1.0]])]});}
            var Q2;
            Q2=makeQuery(id+"F0.imprint","IMPRINT",FACE,{"disambiguationData":[TD([[makeQuery(id+"F0.imprint","IMPRINT",EDGE,{"derivedFrom":sQuery(id+"F0.wireOp",EDGE,"E68")}),-1.0]])]});
            var Q3;
            Q3=makeQuery(id+"F0.imprint","IMPRINT",FACE,{"disambiguationData":[TD([[makeQuery(id+"F0.imprint","IMPRINT",EDGE,{"derivedFrom":sQuery(id+"F0.wireOp",EDGE,"E36")}),1.0]])]});
            extrude(context, id + "F1", {"entities" : qUnion([Q0, Q1, Q2, Q3]), "depth" : 150 * mm, "offsetDistance" : 25 * mm});
        }
    });
